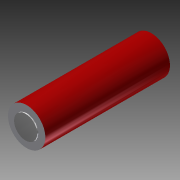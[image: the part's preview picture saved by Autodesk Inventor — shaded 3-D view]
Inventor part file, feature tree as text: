
AUTODESK INVENTOR PART (.ipt)
format: ipt  version: 2016 (Build 200138000, 138)  size: 94,208 bytes
history: native  units: mm
features: revolve x1, sketch x1
ambient origin geometry x8: Origin, YZ Plane, XZ Plane, XY Plane, X Axis, Y Axis, Z Axis, Center Point
bodies: Solid1 (feature_tree)
feature tree (2):
  revolve  "Revolution1"  [1 undecoded]
  sketch  "Sketch2"  dims[d0=50.0mm d1=7.25mm d2=2.5mm d3=1.2mm d4=0.4mm d5=4.5mm d6=90.0deg]
note: 1 required parameter value undecoded (feature->parameter linkage not recoverable at this tier; creation-order binding heuristic only, values carry confidence <= 0.55)
